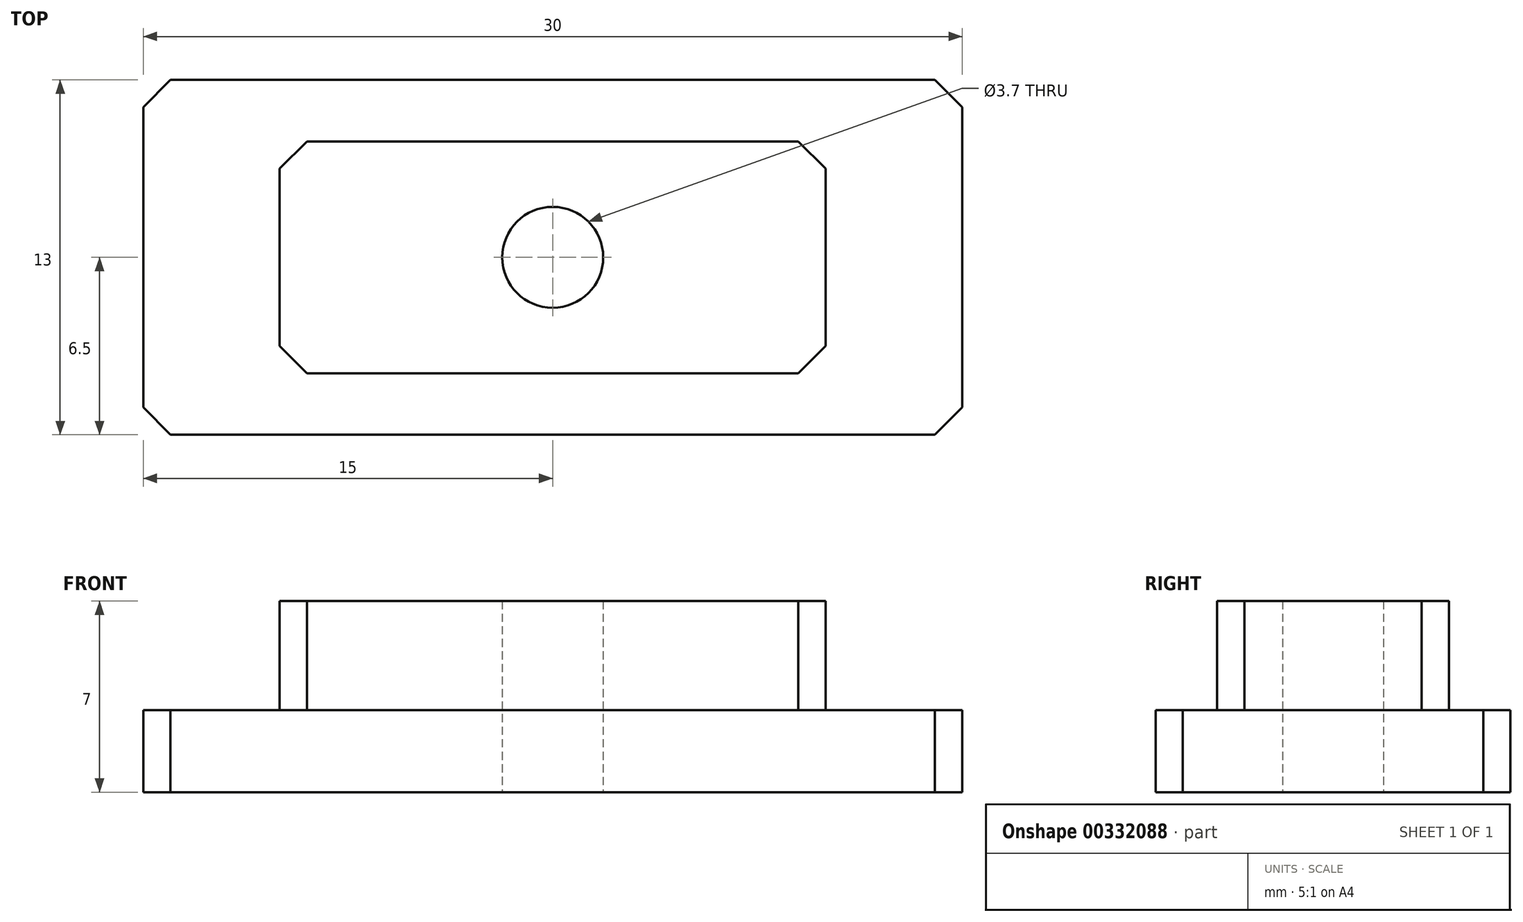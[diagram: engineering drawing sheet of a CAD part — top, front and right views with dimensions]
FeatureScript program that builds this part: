
annotation { "Feature Type Name" : "Feature", "Feature Type Description" : "" }
export const myFeature = defineFeature(function(context is Context, id is Id, definition is map)
    precondition{}
    {
        {
            var Q0;
            Q0=qCreatedBy(makeId("Top.planeOp"),FACE);
            var sketch = newSketch(context, id + "F0", { "sketchPlane" : qUnion([Q0])});
            skLineSegment(sketch, "E0.bottom", {"start": v(15, -6.5) * mm, "end": v(-15, -6.5) * mm});
            skLineSegment(sketch, "E0.top", {"start": v(15, 6.5) * mm, "end": v(-15, 6.5) * mm});
            skLineSegment(sketch, "E0.left", {"start": v(15, -6.5) * mm, "end": v(15, 6.5) * mm});
            skLineSegment(sketch, "E0.right", {"start": v(-15, -6.5) * mm, "end": v(-15, 6.5) * mm});
            skPoint(sketch, "E0.middle", {"position": v(0, 0) * mm});
            skCircle(sketch, "E1", {"center": v(0, 0) * mm, "radius": 1.85 * mm});
            skLineSegment(sketch, "E2.bottom", {"start": v(10, -4.25) * mm, "end": v(-10, -4.25) * mm});
            skLineSegment(sketch, "E2.top", {"start": v(10, 4.25) * mm, "end": v(-10, 4.25) * mm});
            skLineSegment(sketch, "E2.left", {"start": v(10, -4.25) * mm, "end": v(10, 4.25) * mm});
            skLineSegment(sketch, "E2.right", {"start": v(-10, -4.25) * mm, "end": v(-10, 4.25) * mm});
            skSolve(sketch);
        }
        {
            var Q0;
            Q0=makeQuery(id+"F0.imprint","IMPRINT",FACE,{"disambiguationData":[TD([[makeQuery(id+"F0.imprint","IMPRINT",EDGE,{"derivedFrom":sQuery(id+"F0.wireOp",EDGE,"E0.bottom")}),-1.0]])]});
            extrude(context, id + "F1", {"entities" : qUnion([Q0]), "depth" : 3 * mm});
        }
        {
            var Q0;
            Q0=makeQuery(id+"F0.imprint","IMPRINT",FACE,{"disambiguationData":[TD([[makeQuery(id+"F0.imprint","IMPRINT",EDGE,{"derivedFrom":sQuery(id+"F0.wireOp",EDGE,"E1")}),-1.0]])]});
            extrude(context, id + "F2", {"entities" : qUnion([Q0]), "operationType" : NewBodyOperationType.ADD, "depth" : 7 * mm});
        }
        {
            var Q0;
            Q0=makeQuery(id+"F2.opExtrude","SWEPT_EDGE",EDGE,{"disambiguationData":[OSD([sQuery(id+"F0.wireOp",EDGE,"E2.bottom"),sQuery(id+"F0.wireOp",EDGE,"E2.right")])]});
            var Q1;
            Q1=makeQuery(id+"F2.opExtrude","SWEPT_EDGE",EDGE,{"disambiguationData":[OSD([sQuery(id+"F0.wireOp",EDGE,"E2.bottom"),sQuery(id+"F0.wireOp",EDGE,"E2.left")])]});
            var Q2;
            Q2=makeQuery(id+"F2.opExtrude","SWEPT_EDGE",EDGE,{"disambiguationData":[OSD([sQuery(id+"F0.wireOp",EDGE,"E2.top"),sQuery(id+"F0.wireOp",EDGE,"E2.left")])]});
            var Q3;
            Q3=makeQuery(id+"F2.opExtrude","SWEPT_EDGE",EDGE,{"disambiguationData":[OSD([sQuery(id+"F0.wireOp",EDGE,"E2.top"),sQuery(id+"F0.wireOp",EDGE,"E2.right")])]});
            var Q4;
            Q4=makeQuery(id+"F1.opExtrude","SWEPT_EDGE",EDGE,{"disambiguationData":[OSD([sQuery(id+"F0.wireOp",EDGE,"E0.top"),sQuery(id+"F0.wireOp",EDGE,"E0.right")])]});
            var Q5;
            Q5=makeQuery(id+"F1.opExtrude","SWEPT_EDGE",EDGE,{"disambiguationData":[OSD([sQuery(id+"F0.wireOp",EDGE,"E0.top"),sQuery(id+"F0.wireOp",EDGE,"E0.left")])]});
            var Q6;
            Q6=makeQuery(id+"F1.opExtrude","SWEPT_EDGE",EDGE,{"disambiguationData":[OSD([sQuery(id+"F0.wireOp",EDGE,"E0.bottom"),sQuery(id+"F0.wireOp",EDGE,"E0.left")])]});
            var Q7;
            Q7=makeQuery(id+"F1.opExtrude","SWEPT_EDGE",EDGE,{"disambiguationData":[OSD([sQuery(id+"F0.wireOp",EDGE,"E0.bottom"),sQuery(id+"F0.wireOp",EDGE,"E0.right")])]});
            chamfer(context, id + "F3", {"entities" : qUnion([Q0, Q1, Q2, Q3, Q4, Q5, Q6, Q7]), "width" : 1 * mm, "tangentPropagation" : true});
        }
    });
